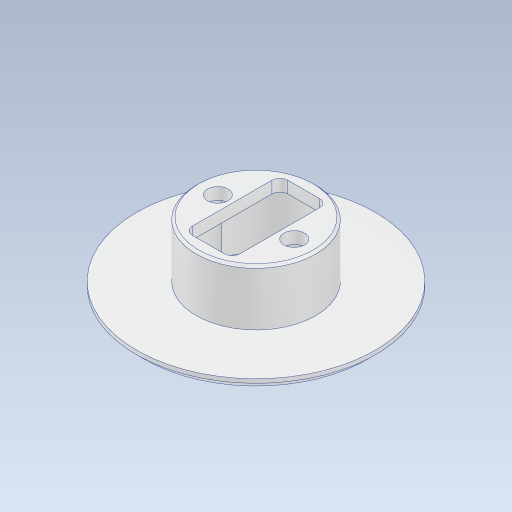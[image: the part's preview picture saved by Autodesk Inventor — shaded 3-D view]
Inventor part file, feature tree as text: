
AUTODESK INVENTOR PART (.ipt)
format: ipt  version: 2024 (Build 280153000, 153)  size: 196,608 bytes
history: native  units: mm
features: other x5, extrude x3, chamfer x2, sketch x1
ambient origin geometry x8: Origin, YZ Plane, XZ Plane, XY Plane, X Axis, Y Axis, Z Axis, Center Point
bodies: Body1 (feature_tree)
feature tree (11):
  other  "_bridseye_sketch.ipt"
  sketch  "スケッチ4"
  extrude  "押し出し1"  Depth=10.0mm
  extrude  "押し出し2"  Depth=10.0mm TaperAngle=0.0deg
  extrude  "押し出し3"  TaperAngle=0.0deg  [1 undecoded]
  chamfer  "面取り2"  Distance=10.0mm
  chamfer  "面取り3"  Distance=1.0mm Angle=45.0deg
  other  "TaggingFeature1"
  other  "ソリッド8::_bridseye_sketch.ipt"
  other  "front_shoulderUnit"
  other  "top_shoulderUnit-largeGearShaft_baseWasher"
note: 1 required parameter value undecoded (feature->parameter linkage not recoverable at this tier; creation-order binding heuristic only, values carry confidence <= 0.55)
